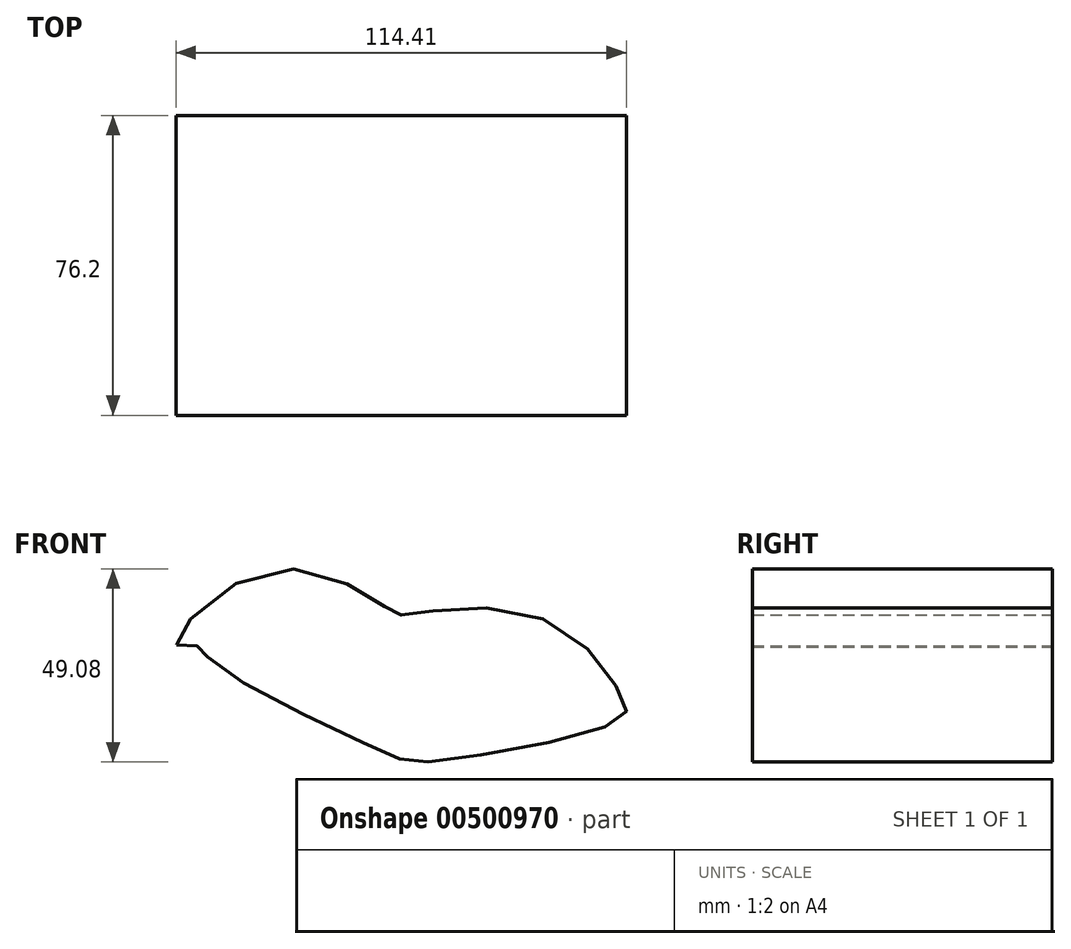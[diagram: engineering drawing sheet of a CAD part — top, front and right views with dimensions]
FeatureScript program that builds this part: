
annotation { "Feature Type Name" : "Feature", "Feature Type Description" : "" }
export const myFeature = defineFeature(function(context is Context, id is Id, definition is map)
    precondition{}
    {
        {
            var Q0;
            Q0=qCreatedBy(makeId("Front.planeOp"),FACE);
            var sketch = newSketch(context, id + "F0", { "sketchPlane" : qUnion([Q0])});
            skFitSpline(sketch, "E0", {"points": [v(-55.69, -19) * mm, v(-31.63, 0) * mm, v(-1.2, -10.37) * mm, v(2.13, -11.3) * mm, v(36.55, -11.96) * mm, v(57.95, -33.36) * mm, v(56.75, -38.14) * mm, v(9.57, -48.51) * mm, v(-4.25, -45.72) * mm, v(-47.58, -22.2) * mm, v(-49.84, -19.27) * mm, v(-55.69, -19) * mm]});
            skSolve(sketch);
        }
        {
            var Q0;
            Q0 = qSketchRegion(id + "F0", true);
            extrude(context, id + "F1", {"entities" : qUnion([Q0]), "depth" : 76.2 * mm});
        }
    });
